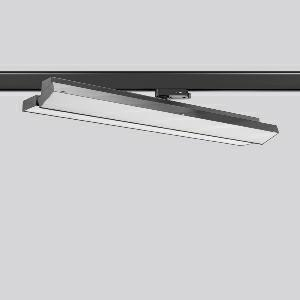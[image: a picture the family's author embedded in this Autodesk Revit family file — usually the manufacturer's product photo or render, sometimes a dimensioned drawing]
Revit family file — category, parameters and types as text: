
# Revit family: tx-move_742164_003_3_2480
name_source: partatom
category: Lighting Fixtures
units: mm (PartAtom-declared; Revit-internal decimal feet)

## family parameters
Cut with Voids When Loaded = No
Host = Face
Light Source = No
Part Type = Normal
Room Calculation Point = No
Round Connector Dimension = Use Diameter
Shared = No

## types (1)
- MultiLumen 1 (1 x LED Modul 835, 2550 lm, 3500)
    Apparent Load = 41 VA
    CIE Flux Codes = 47 79 96 100 100
    Color Rendering = 80
    Color Temperature = 3500
    Default Elevation = 1800 mm
    Description = Series: TX-MOVE
Multifunctional surface-mounted spotlight for area lighting. Very flat design. Housing: sheet steel, powder-coated. Rotation range: 356°. Swivel range: 90°. Consistent alignment possible with visible tilt scale. High-efficiency LED units with flush-mounted opal diffuser made of non-yellowing PMMA. Symmetrical wide beam light emission. With multi adaptor for 3-circuit tracks 230 V. Suitable for Track on ceiling. MultiLumen: Luminous flux adjustable in 3 steps. Factory setting is the highest luminous flux. Environmentally friendly and resource-saving due to replaceable and recyclable components. 
Colour: deep black, matt (RAL 9005)
Length: 570 mm
Width: 119 mm
Height: 92 mm
Lamp: LED
Socket: without socket
Colour temperature: 3500K
Colour rendering index (CRI): 80
System power: 41 W
Rated luminous flux: 5100 lm
Luminous efficiency: 124 lm/W
System power 2: 57 W
Rated luminous flux 2: 6950 lm
Luminous efficiency 2: 122 lm/W
System power 3: 73 W
Rated luminous flux 3: 8500 lm
Luminous efficiency 3: 116 lm/W
Control gear: Regulated power supply
Protection class: I
Type of protection: IP 20
    Height = 75 mm
    Lamp = 1 x LED Modul 835
    Lamp Light Flux = 2550 lm
    Lamp count = 1
    Length = 569 mm
    Lifetime = 50000 h
    Luminous efficacy = 124 lm/W
    Manufacturer = RZB
    ModVariant = No
    Model = 742164.003.3
    Mounting Place = Ceiling
    Mounting Type = Rail mounted
    Number of Poles = 1
    OnlyDefault = Yes
    Power Factor = 1
    Product Name = TX-MOVE
    Product group = Track mounted projectors
    ProductGroupID = 301
    Protection Class = Protection class I
    Protection Degree = IP 20
    RLX_Detail_Level = 1
    RLX_Emergency_Light_Flux = 0 lm
    RLX_Emergency_Type = 0
    RLX_Emergency_Type_DB = No
    RlxData = <blob elided: 35581 chars, md5=b416c8c0>
    Socket = socket
    Standby Power = 0 W
    System Light Flux = 5100 lm
    System Power = 41 W
    Type Comments = MultiLumen 1
    Type Image = 742164.003.jpg
    URL = http://relux.com
    VarID = multilumen_1
    Voltage = 230 V
    Voltage Range = 220-240 V
    Weight = 0.00 kg
    Width = 119 mm

## geometry (parser evidence)
native form markers: Blend x4, Sweep x15
no freeform markers — native parametric forms only
